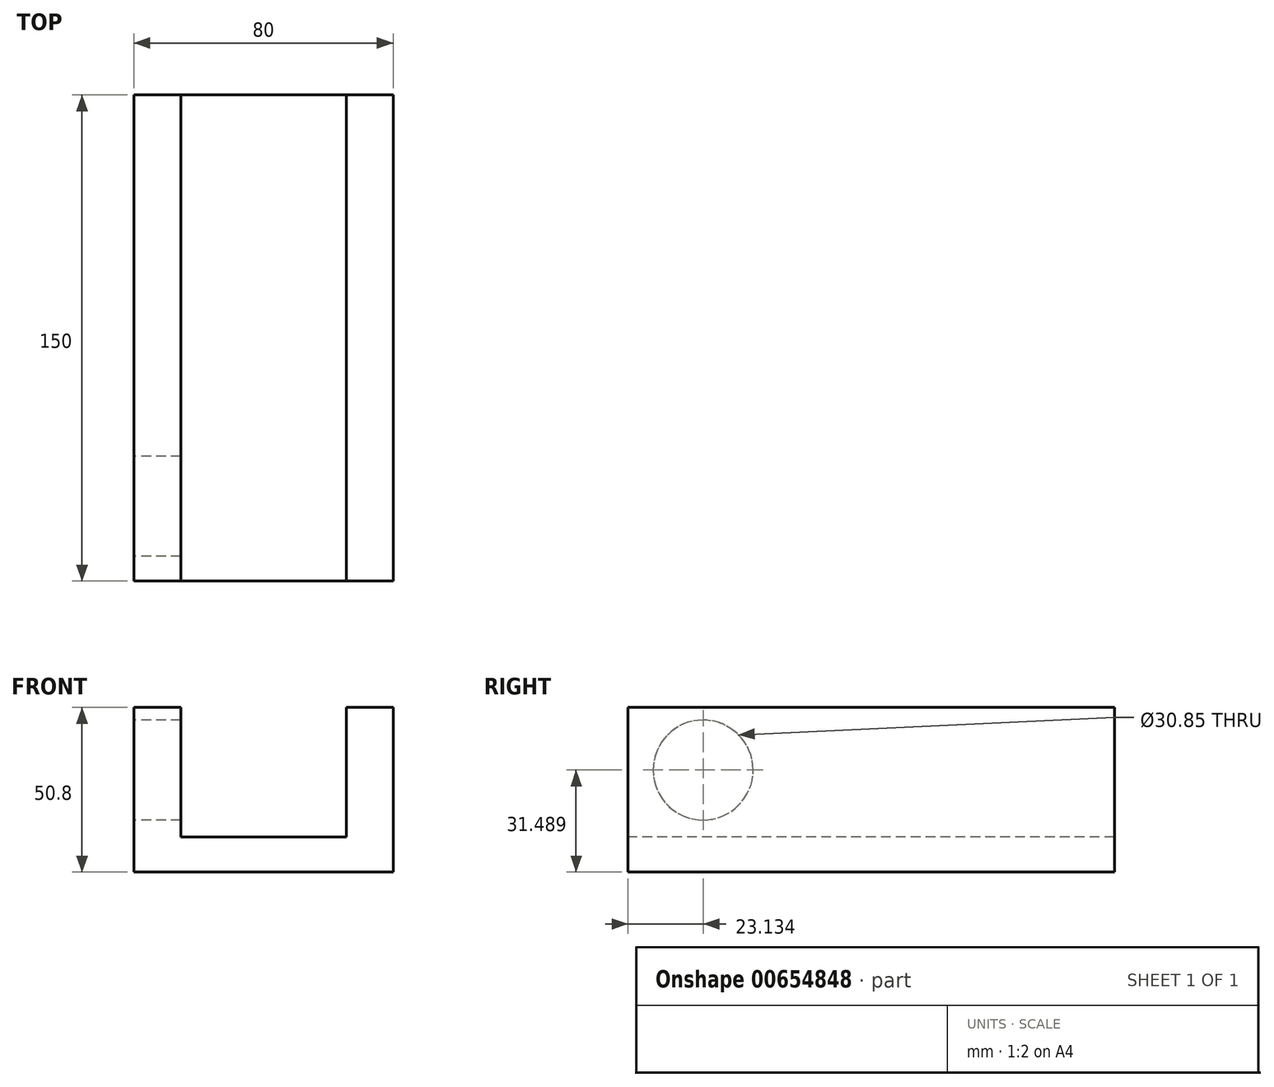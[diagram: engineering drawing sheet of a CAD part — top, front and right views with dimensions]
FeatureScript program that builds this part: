
annotation { "Feature Type Name" : "Feature", "Feature Type Description" : "" }
export const myFeature = defineFeature(function(context is Context, id is Id, definition is map)
    precondition{}
    {
        {
            var Q0;
            Q0=qCreatedBy(makeId("Right.planeOp"),FACE);
            var sketch = newSketch(context, id + "F0", { "sketchPlane" : qUnion([Q0])});
            skLineSegment(sketch, "E0.bottom", {"start": v(-59.67, 50.8) * mm, "end": v(90.33, 50.8) * mm});
            skLineSegment(sketch, "E0.top", {"start": v(-59.67, 0) * mm, "end": v(90.33, 0) * mm});
            skLineSegment(sketch, "E0.left", {"start": v(-59.67, 50.8) * mm, "end": v(-59.67, 0) * mm});
            skLineSegment(sketch, "E0.right", {"start": v(90.33, 50.8) * mm, "end": v(90.33, 0) * mm});
            skSolve(sketch);
        }
        {
            var Q0;
            Q0=makeQuery(id+"F0.imprint","IMPRINT",FACE,{"disambiguationData":[TD([[makeQuery(id+"F0.imprint","IMPRINT",EDGE,{"derivedFrom":sQuery(id+"F0.wireOp",EDGE,"E0.bottom")}),-1.0]])]});
            extrude(context, id + "F1", {"entities" : qUnion([Q0]), "oppositeDirection" : true, "depth" : -80 * mm, "offsetDistance" : 25.4 * mm});
        }
        {
            var Q0;
            Q0=makeQuery(id+"F1.opExtrude","SWEPT_FACE",FACE,{"disambiguationData":[OSD([sQuery(id+"F0.wireOp",EDGE,"E0.bottom")])]});
            var sketch = newSketch(context, id + "F2", { "sketchPlane" : qUnion([Q0])});
            skLineSegment(sketch, "E1.bottom", {"start": v(14.5, 90.33) * mm, "end": v(65.5, 90.33) * mm});
            skLineSegment(sketch, "E1.top", {"start": v(14.5, -59.67) * mm, "end": v(65.5, -59.67) * mm});
            skLineSegment(sketch, "E1.left", {"start": v(14.5, 90.33) * mm, "end": v(14.5, -59.67) * mm});
            skLineSegment(sketch, "E1.right", {"start": v(65.5, 90.33) * mm, "end": v(65.5, -59.67) * mm});
            skSolve(sketch);
        }
        {
            var Q0;
            Q0 = qSketchRegion(id + "F2", true);
            extrude(context, id + "F3", {"entities" : qUnion([Q0]), "operationType" : NewBodyOperationType.REMOVE, "oppositeDirection" : true, "depth" : 40 * mm, "offsetDistance" : 25.4 * mm});
        }
        {
            var Q0;
            Q0=makeQuery(id+"F0.imprint","IMPRINT",FACE,{"disambiguationData":[TD([[makeQuery(id+"F0.imprint","IMPRINT",EDGE,{"derivedFrom":sQuery(id+"F0.wireOp",EDGE,"E0.bottom")}),-1.0]])]});
            var sketch = newSketch(context, id + "F4", { "sketchPlane" : qUnion([Q0])});
            skCircle(sketch, "E2", {"center": v(-36.54, 31.49) * mm, "radius": 15.43 * mm});
            skSolve(sketch);
        }
        {
            var Q0;
            Q0 = qSketchRegion(id + "F4", true);
            extrude(context, id + "F5", {"entities" : qUnion([Q0]), "operationType" : NewBodyOperationType.REMOVE, "depth" : 25.4 * mm, "offsetDistance" : 25.4 * mm});
        }
    });
